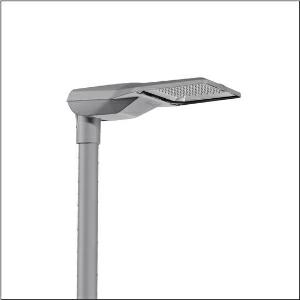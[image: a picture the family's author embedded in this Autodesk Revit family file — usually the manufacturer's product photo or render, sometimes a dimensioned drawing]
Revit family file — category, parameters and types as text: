
# Revit family: streetlight_sl_21_iq_midi___st0_8a_5xe3c21g08nb_deda
name_source: partatom
category: Lighting Fixtures
units: mm (PartAtom-declared; Revit-internal decimal feet)

## family parameters
Cut with Voids When Loaded = No
Host = Face
Light Source = No
Part Type = Normal
Room Calculation Point = No
Round Connector Dimension = Use Diameter
Shared = No

## types (1)
- --- (1 x LED, 19210 lm, 155.5 W, 2200K)
    Apparent Load = 155 VA
    CIE Flux Codes = 41 75 97 100 100
    Color Rendering = 70
    Color Temperature = 2200K
    Default Elevation = 1800 mm
    Description = Streetlight SL 21 iQ midi, mast luminaire, primary light control with lens, of PMMA, primary optical cover: cover, of toughened safety glass, transparent, light distribution: ST0.8a, light emission: direct distribution, primary light characteristic: asymmetric, installation type: post-top, side-entry, LED, High Power LED, rated luminous flux: 19.210lm, luminous efficacy: 124lm/W, light colour: 722, colour temperature: 2200K, control: Street-Remote, Auto-Match, Temp-Guard, Lumen-Switch, Night-Set, Smart-Wire, Light-Fading, Desk-Remote (wireless, voltage-free reading and setting of iQ features in the workshop via application-optimized NFC function/RFID function), optimised constant luminous flux control (CLO 2.0), presetting dimming linear, mains connection: 230..240V, AC, 50/60Hz, start of lifetime: 156W, end of service life: 162W, reduction: 69W, luminaire housing, of diecast aluminium, powder-coated, Siteco® metallic grey (DB 702S), corrosivity category C5 mid according to DIN EN ISO 12944, please order mast flange separately, inclination adjustable: 0°, 5°, 10°, 15°, sealing non-destructively replaceable, multi-level sealing system, length: 644mm, width: 335mm, height: 110mm, mast flange for spigot size: 42mm (side-entry): 5XC10008XM4, 60/48mm (side-entry/post-top): 5XC10108XM2, 76/60mm (side-entry/post-top): 5XC10108XM1, protection rating (complete): IP66, insulation class (complete): insulation class II (safety insulation), certification: CE, ENEC, ENEC+, VDE, impact resistance: IK09, permissible operating ambient temperature for outdoor applications: -40..+50°C, standard-compliant lighting for roads and squares, packaging unit: 1 piece

Light Distribution: ST0.8a
    Height = 111 mm
    Lamp = 1 x LED
    Lamp Light Flux = 19210 lm
    Lamp Power = 155.5 W
    Lamp count = 1
    Length = 644 mm
    Luminous efficacy = 124 lm/W
    Manufacturer = Siteco
    ModVariant = No
    Model = 5XE3C21G08NB
    Number of Poles = 1
    OnlyDefault = Yes
    Power Factor = 1
    Product Name = Streetlight SL 21 iQ midi | ST0.8a
    Product group = mast luminaire | pylon top
    ProductGroupID = 6100
    Protection Class = Protection class II
    Protection Degree = IP 66
    RLX_Detail_Level = 1
    RLX_Emergency_Light_Flux = 0 lm
    RLX_Emergency_Type = 0
    RLX_Emergency_Type_DB = No
    RlxData = <blob elided: 91309 chars, md5=d48546fb>
    Socket = socket
    Standby Power = 0 W
    System Light Flux = 19210 lm
    System Power = 155 W
    Type Comments = factory setting: luminous flux: 100 % | dim-lin: 254 | 823 mA
    Type Image = l_1004298.jpg
    URL = http://relux.com
    VarID = @adj_119317
    Voltage = 0 V
    Weight = 0.00 kg
    Width = 336 mm

## geometry (parser evidence)
native form markers: Blend x4, Sweep x11
no freeform markers — native parametric forms only
